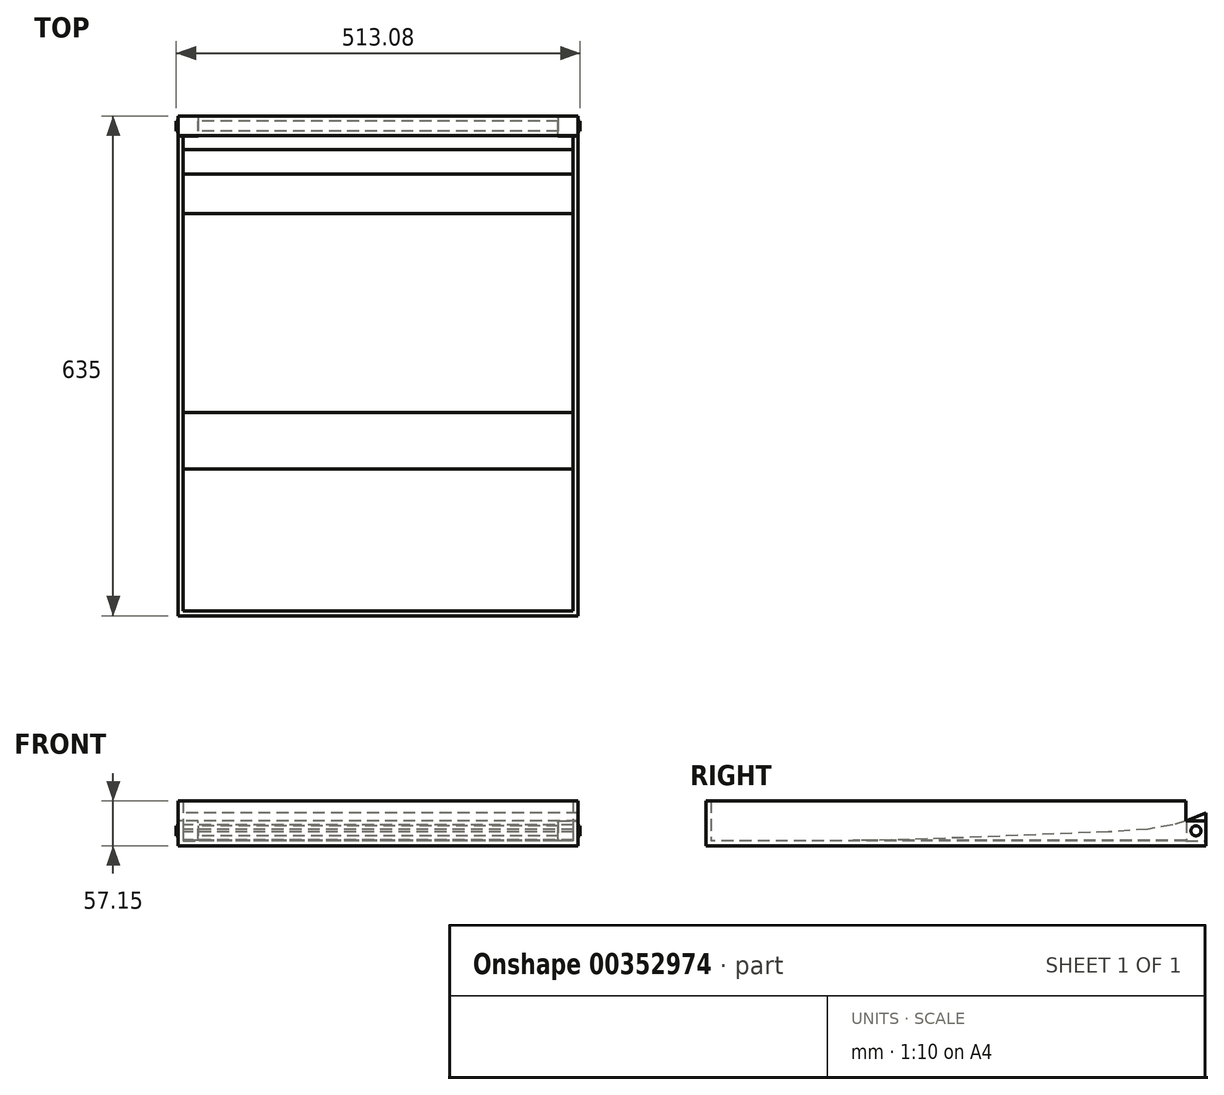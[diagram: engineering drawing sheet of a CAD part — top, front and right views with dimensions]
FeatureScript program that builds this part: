
annotation { "Feature Type Name" : "Feature", "Feature Type Description" : "" }
export const myFeature = defineFeature(function(context is Context, id is Id, definition is map)
    precondition{}
    {
        {
            var Q0;
            Q0=qCreatedBy(makeId("Top.planeOp"),FACE);
            var sketch = newSketch(context, id + "F0", { "sketchPlane" : qUnion([Q0])});
            skLineSegment(sketch, "E0.bottom", {"start": v(254, -317.5) * mm, "end": v(-254, -317.5) * mm});
            skLineSegment(sketch, "E0.top", {"start": v(254, 317.5) * mm, "end": v(-254, 317.5) * mm});
            skLineSegment(sketch, "E0.left", {"start": v(254, -317.5) * mm, "end": v(254, 317.5) * mm});
            skLineSegment(sketch, "E0.right", {"start": v(-254, -317.5) * mm, "end": v(-254, 317.5) * mm});
            skPoint(sketch, "E0.middle", {"position": v(0, 0) * mm});
            skSolve(sketch);
        }
        {
            var Q0;
            Q0 = qSketchRegion(id + "F0", true);
            extrude(context, id + "F1", {"entities" : qUnion([Q0]), "depth" : 6.35 * mm});
        }
        {
            var Q0;
            Q0=makeQuery(id+"F1.opExtrude","SWEPT_FACE",FACE,{"disambiguationData":[OSD([sQuery(id+"F0.wireOp",EDGE,"E0.left")])]});
            var sketch = newSketch(context, id + "F2", { "sketchPlane" : qUnion([Q0])});
            skLineSegment(sketch, "E1.bottom", {"start": v(317.5, 0) * mm, "end": v(292.1, 0) * mm});
            skLineSegment(sketch, "E1.top", {"start": v(317.5, 31.75) * mm, "end": v(292.1, 31.75) * mm});
            skLineSegment(sketch, "E1.left", {"start": v(317.5, 0) * mm, "end": v(317.5, 31.75) * mm});
            skLineSegment(sketch, "E1.right", {"start": v(292.1, 0) * mm, "end": v(292.1, 31.75) * mm});
            skSolve(sketch);
        }
        {
            var Q0;
            Q0 = qSketchRegion(id + "F2", true);
            extrude(context, id + "F3", {"entities" : qUnion([Q0]), "operationType" : NewBodyOperationType.ADD, "oppositeDirection" : true, "depth" : 25.4 * mm});
        }
        {
            var Q0;
            Q0=makeQuery(id+"F1.opExtrude","SWEPT_FACE",FACE,{"disambiguationData":[OSD([sQuery(id+"F0.wireOp",EDGE,"E0.right")])]});
            var sketch = newSketch(context, id + "F4", { "sketchPlane" : qUnion([Q0])});
            skLineSegment(sketch, "E2.bottom", {"start": v(-317.5, 0) * mm, "end": v(-292.1, 0) * mm});
            skLineSegment(sketch, "E2.top", {"start": v(-317.5, 31.75) * mm, "end": v(-292.1, 31.75) * mm});
            skLineSegment(sketch, "E2.left", {"start": v(-317.5, 0) * mm, "end": v(-317.5, 31.75) * mm});
            skLineSegment(sketch, "E2.right", {"start": v(-292.1, 0) * mm, "end": v(-292.1, 31.75) * mm});
            skSolve(sketch);
        }
        {
            var Q0;
            Q0 = qSketchRegion(id + "F4", true);
            extrude(context, id + "F5", {"entities" : qUnion([Q0]), "operationType" : NewBodyOperationType.ADD, "oppositeDirection" : true, "depth" : 25.4 * mm});
        }
        {
            var Q0;
            Q0=makeQuery(id+"F3.boolean.opBoolean","MERGE",FACE,{"derivedFrom":[makeQuery(id+"F1.opExtrude","SWEPT_FACE",FACE,{"disambiguationData":[OSD([sQuery(id+"F0.wireOp",EDGE,"E0.left")])]}),makeQuery(id+"F3.opExtrude","CAP_FACE",FACE,{"disambiguationData":[OSD([sQuery(id+"F2.wireOp",EDGE,"E1.bottom"),sQuery(id+"F2.wireOp",EDGE,"E1.top"),sQuery(id+"F2.wireOp",EDGE,"E1.left"),sQuery(id+"F2.wireOp",EDGE,"E1.right")])],"isStart":true})]});
            var sketch = newSketch(context, id + "F6", { "sketchPlane" : qUnion([Q0])});
            skCircle(sketch, "E3", {"center": v(304.8, 19.05) * mm, "radius": 6.35 * mm});
            skSolve(sketch);
        }
        {
            var Q0;
            Q0 = qSketchRegion(id + "F6", true);
            extrude(context, id + "F7", {"entities" : qUnion([Q0]), "operationType" : NewBodyOperationType.ADD, "depth" : 2.54 * mm, "hasSecondDirection" : true, "secondDirectionOppositeDirection" : true, "secondDirectionDepth" : 510.54 * mm});
        }
        {
            var Q0;
            Q0=qCreatedBy(makeId("Right.planeOp"),FACE);
            var sketch = newSketch(context, id + "F8", { "sketchPlane" : qUnion([Q0])});
            skLineSegment(sketch, "E4", {"start": v(-130.77, 6.8) * mm, "end": v(-59.11, 7.67) * mm});
            skLineSegment(sketch, "E5", {"start": v(-59.11, 7.67) * mm, "end": v(-19.84, 9.23) * mm});
            skLineSegment(sketch, "E6", {"start": v(-19.84, 9.23) * mm, "end": v(20.21, 10.82) * mm});
            skLineSegment(sketch, "E7", {"start": v(20.21, 10.82) * mm, "end": v(55.37, 12.22) * mm});
            skLineSegment(sketch, "E8", {"start": v(55.37, 12.22) * mm, "end": v(134.05, 15.34) * mm});
            skLineSegment(sketch, "E9", {"start": v(134.05, 15.34) * mm, "end": v(193.38, 17.7) * mm});
            skLineSegment(sketch, "E10", {"start": v(193.38, 17.7) * mm, "end": v(243.85, 21.17) * mm});
            skLineSegment(sketch, "E11", {"start": v(243.85, 21.17) * mm, "end": v(275.12, 26.36) * mm});
            skLineSegment(sketch, "E12", {"start": v(275.12, 26.36) * mm, "end": v(292.64, 31.81) * mm});
            skLineSegment(sketch, "E13", {"start": v(292.64, 31.81) * mm, "end": v(317.42, 42.09) * mm});
            skLineSegment(sketch, "E14", {"start": v(-130.77, 6.8) * mm, "end": v(292.28, 6.8) * mm});
            skLineSegment(sketch, "E15", {"start": v(292.28, 6.8) * mm, "end": v(292.64, 31.81) * mm});
            skLineSegment(sketch, "E16", {"start": v(317.44, 31.81) * mm, "end": v(317.42, 42.09) * mm});
            skLineSegment(sketch, "E17", {"start": v(292.64, 31.81) * mm, "end": v(317.44, 31.81) * mm});
            skSolve(sketch);
        }
        {
            var Q0;
            Q0=makeQuery(id+"F8.imprint","IMPRINT",FACE,{"disambiguationData":[TD([[makeQuery(id+"F8.imprint","IMPRINT",EDGE,{"derivedFrom":sQuery(id+"F8.wireOp",EDGE,"E4")}),-1.0]])]});
            var Q1;
            Q1=makeQuery(id+"F8.imprint","IMPRINT",FACE,{"disambiguationData":[TD([[makeQuery(id+"F8.imprint","IMPRINT",EDGE,{"derivedFrom":sQuery(id+"F8.wireOp",EDGE,"E13")}),-1.0]])]});
            extrude(context, id + "F9", {"entities" : qUnion([Q0, Q1]), "operationType" : NewBodyOperationType.ADD, "depth" : 254 * mm, "hasSecondDirection" : true, "secondDirectionOppositeDirection" : true, "secondDirectionDepth" : 254 * mm});
        }
        {
            var Q0;
            Q0=makeQuery(id+"F1.opExtrude","CAP_FACE",FACE,{"disambiguationData":[OSD([sQuery(id+"F0.wireOp",EDGE,"E0.bottom"),sQuery(id+"F0.wireOp",EDGE,"E0.top"),sQuery(id+"F0.wireOp",EDGE,"E0.left"),sQuery(id+"F0.wireOp",EDGE,"E0.right")])],"isStart":true});
            var sketch = newSketch(context, id + "F10", { "sketchPlane" : qUnion([Q0])});
            skLineSegment(sketch, "E18.bottom", {"start": v(-254, 317.5) * mm, "end": v(-247.65, 317.5) * mm});
            skLineSegment(sketch, "E18.top", {"start": v(-254, -292.1) * mm, "end": v(-247.65, -292.1) * mm});
            skLineSegment(sketch, "E18.left", {"start": v(-254, 317.5) * mm, "end": v(-254, -292.1) * mm});
            skLineSegment(sketch, "E18.right", {"start": v(-247.65, 317.5) * mm, "end": v(-247.65, -292.1) * mm});
            skLineSegment(sketch, "E19.bottom", {"start": v(-254, 317.5) * mm, "end": v(254, 317.5) * mm});
            skLineSegment(sketch, "E19.top", {"start": v(-254, 311.15) * mm, "end": v(254, 311.15) * mm});
            skLineSegment(sketch, "E19.left", {"start": v(-254, 317.5) * mm, "end": v(-254, 311.15) * mm});
            skLineSegment(sketch, "E19.right", {"start": v(254, 317.5) * mm, "end": v(254, 311.15) * mm});
            skLineSegment(sketch, "E20.bottom", {"start": v(254, 317.5) * mm, "end": v(247.65, 317.5) * mm});
            skLineSegment(sketch, "E20.top", {"start": v(254, -292.1) * mm, "end": v(247.65, -292.1) * mm});
            skLineSegment(sketch, "E20.left", {"start": v(254, 317.5) * mm, "end": v(254, -292.1) * mm});
            skLineSegment(sketch, "E20.right", {"start": v(247.65, 317.5) * mm, "end": v(247.65, -292.1) * mm});
            skSolve(sketch);
        }
        {
            var Q0;
            Q0 = qSketchRegion(id + "F10", true);
            extrude(context, id + "F11", {"entities" : qUnion([Q0]), "operationType" : NewBodyOperationType.ADD, "oppositeDirection" : true, "depth" : 57.15 * mm});
        }
    });
